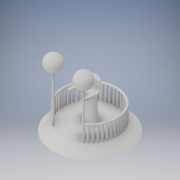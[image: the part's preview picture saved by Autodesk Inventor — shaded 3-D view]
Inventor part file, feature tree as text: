
AUTODESK INVENTOR PART (.ipt)
format: ipt  version: 2017 (Build 210142000, 142)  size: 880,128 bytes
history: native  units: in
note: dims shown in document units (in); Inventor stores cm internally (conversion verified against a paired STEP export)
features: other x22, sketch x14, extrude x9, loft x2, plane x1, fillet x1
ambient origin geometry x7: Origin, YZ Plane, XY Plane, X Axis, Y Axis, Z Axis, Center Point
bodies: Body1 (feature_tree)
feature tree (49):
  other  "bace + terminal"
  other  "bace of terminal"
  other  "middle workplane"
  other  "middle"
  other  "top workplane"
  loft  "curved tower"
  extrude  "arm rests and terminal monitor"  Depth=0.8in
  other  "middle of the part vertical"
  other  "used to line up the key board and mouse"
  extrude  "bace"  Depth=1.8247in
  other  "ramp around"
  extrude  "railing bars"  Depth=1.0in
  other  "railing bar top workplane"
  other  "railing bar top"
  extrude  "light pole"  Depth=1.2in
  other  "globe light workplane"
  sketch  "Sketch20"  dims[d20=0.85in d27=1.1in]
  other  "light 1"
  other  "light 2"
  extrude  "line up slot"  Depth=1.1in
  other  "mate to back to monitor"
  extrude  "monitor raise"  Depth=1.0in
  sketch  "Sketch26"  dims[d123=1.0in d124=0.0in d134=0.7579in]
  plane  "Work Plane16"
  loft  "outlet cap"
  sketch  "Sketch28"  dims[d141=0.2749in d142=90.0deg d143=0.25in]
  extrude  "outlet revele out"  Depth=0.7579in
  extrude  "hot and ground wire holes"  Depth=2.0in TaperAngle=0.0deg
  other  "screw workplane"
  other  "screw made"
  extrude  "slot for screw"  TaperAngle=90.0deg  [1 undecoded]
  fillet  "Fillet3"  Radius=0.25in
  other  "bottom workplane"
  other  "top"
  sketch  "Sketch15"  dims[d0=1.0in d1=0.75in]
  sketch  "Sketch16"  dims[d2=1.8247in d3=0.8in]
  sketch  "Sketch17"  dims[d4=0.55in d5=1.8247in]
  other  "Work Axis3"
  other  "Work Axis4"
  sketch  "Sketch18"  dims[d6=0.75in d7=1.0in]
  sketch  "Sketch19"  dims[d8=0.0in d9=90.0deg d10=0.0in d11=90.0deg d12=0.0in d13=90.0deg d19=1.2in]
  other  "Work Axis5"
  other  "Work Axis6"
  sketch  "Sketch21"  dims[d28=0.75in d29=1.0in]
  sketch  "Sketch23"  dims[d30=0.65in]
  sketch  "Sketch25"  dims[d42=1.1in d43=0.85in d44=1.0in d45=0.75in d49=1.2in d50=0.85in d51=1.0in d52=0.75in d122=7.0in]
  sketch  "Sketch27"  dims[d135=15.748in d137=1.9948in d139=2.0in d140=0.0in]
  sketch  "Sketch29"  dims[d144=0.25in]
  sketch  "Sketch30"  dims[d145=90.0deg d146=4.0in d147=0.0in d150=2.0in d151=0.9in d152=2.0in d153=0.9in d155=90.0deg d156=90.0deg d157=0.0in d158=2.0in d159=0.2in d160=0.0in d163=0.8125in d165=0.4167in d166=0.8125in d167=0.4167in d168=0.2083in d169=0.0in d170=1.125in d173=1.8892in d174=1.1844in d175=1.125in d176=1.125in d177=1.1844in d178=1.0in d179=0.0in d180=0.5527in d181=0.01in d182=0.2318in d183=0.3777in d184=0.05in d185=0.0181in d186=0.0678in d187=0.1962in d188=0.3421in d189=0.05in d190=0.2318in d191=0.3777in d192=0.0in d193=90.0deg d194=0.0in d195=90.0deg d196=0.0251in d197=0.0305in d198=0.0931in d199=0.0311in d200=0.0362in d201=0.0045in d202=0.0208in d203=0.0208in d204=0.0078in d205=0.0291in d206=0.0078in d207=0.0362in d208=0.0045in d209=0.0208in d210=0.0078in d211=0.0078in d212=0.0208in d213=0.0181in d214=0.0291in d215=0.003in d216=0.0in d217=0.0649in d218=0.0in d219=90.0deg d220=0.0108in d221=0.0027in d222=90.0deg d223=0.0015in d224=0.0128in d225=0.0in]
note: 1 required parameter value undecoded (feature->parameter linkage not recoverable at this tier; creation-order binding heuristic only, values carry confidence <= 0.55)
